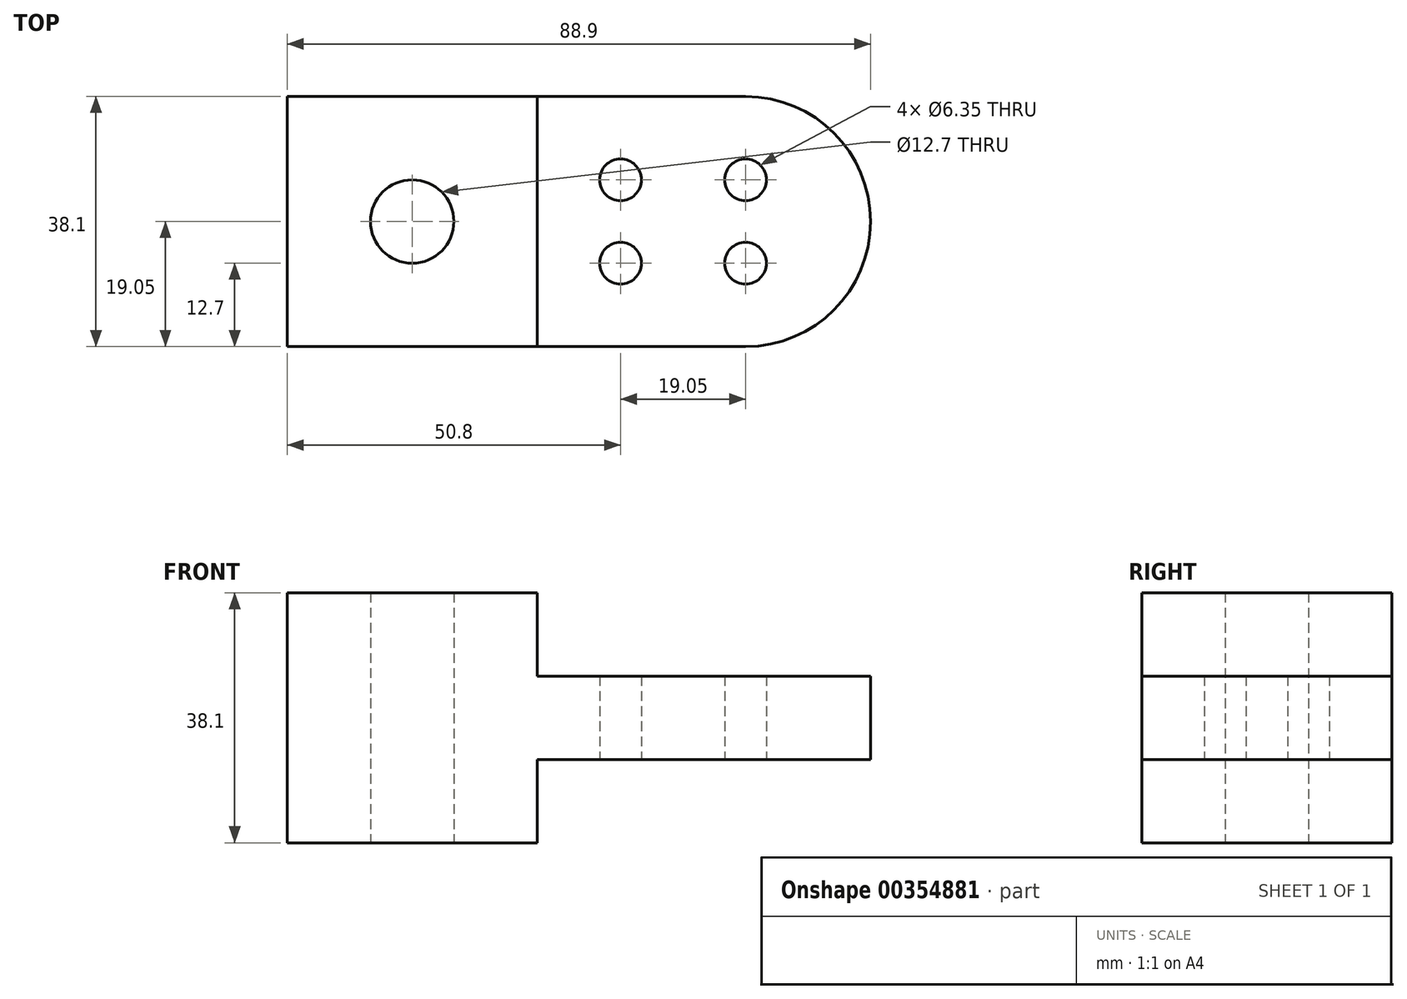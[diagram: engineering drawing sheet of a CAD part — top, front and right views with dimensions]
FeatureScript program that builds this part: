
annotation { "Feature Type Name" : "Feature", "Feature Type Description" : "" }
export const myFeature = defineFeature(function(context is Context, id is Id, definition is map)
    precondition{}
    {
        {
            var Q0;
            Q0=qCreatedBy(makeId("Top.planeOp"),FACE);
            var sketch = newSketch(context, id + "F0", { "sketchPlane" : qUnion([Q0])});
            skLineSegment(sketch, "E0", {"start": v(-19.05, -19.05) * mm, "end": v(-19.05, 19.05) * mm});
            skLineSegment(sketch, "E1", {"start": v(-19.05, 19.05) * mm, "end": v(19.05, 19.05) * mm});
            skLineSegment(sketch, "E2", {"start": v(19.05, 19.05) * mm, "end": v(19.05, -19.05) * mm});
            skLineSegment(sketch, "E3", {"start": v(19.05, -19.05) * mm, "end": v(-19.05, -19.05) * mm});
            skLineSegment(sketch, "E4", {"start": v(19.05, 19.05) * mm, "end": v(50.8, 19.05) * mm});
            skLineSegment(sketch, "E5", {"start": v(50.8, 19.05) * mm, "end": v(50.8, -19.05) * mm});
            skLineSegment(sketch, "E6", {"start": v(50.8, -19.05) * mm, "end": v(19.05, -19.05) * mm});
            skCircle(sketch, "E7", {"center": v(0, 0) * mm, "radius": 6.35 * mm});
            skCircle(sketch, "E8", {"center": v(31.75, 6.35) * mm, "radius": 3.18 * mm});
            skCircle(sketch, "E9", {"center": v(50.8, 6.35) * mm, "radius": 3.18 * mm});
            skCircle(sketch, "E10", {"center": v(50.8, -6.35) * mm, "radius": 3.18 * mm});
            skCircle(sketch, "E11", {"center": v(31.75, -6.35) * mm, "radius": 3.18 * mm});
            skArc(sketch, "E12", {"start": v(50.8, -19.05) * mm, "mid": v(69.85, 0) * mm, "end": v(50.8, 19.05) * mm});
            skSolve(sketch);
        }
        {
            var Q0;
            Q0=makeQuery(id+"F0.imprint","IMPRINT",FACE,{"disambiguationData":[TD([[makeQuery(id+"F0.imprint","IMPRINT",EDGE,{"derivedFrom":sQuery(id+"F0.wireOp",EDGE,"E0")}),-1.0]])]});
            extrude(context, id + "F1", {"entities" : qUnion([Q0]), "endBound" : BoundingType.SYMMETRIC, "depth" : 38.1 * mm});
        }
        {
            var Q0;
            Q0=makeQuery(id+"F0.imprint","IMPRINT",FACE,{"disambiguationData":[TD([[makeQuery(id+"F0.imprint","IMPRINT",EDGE,{"derivedFrom":sQuery(id+"F0.wireOp",EDGE,"E2")}),1.0]])]});
            var Q1;
            {var subQ4=sQuery(id+"F0.wireOp",EDGE,"E12");Q1=makeQuery(id+"F0.imprint","IMPRINT",FACE,{"disambiguationData":[TD([[makeQuery(id+"F0.imprint","IMPRINT",EDGE,{"derivedFrom":subQ4}),1.0]])]});}
            extrude(context, id + "F2", {"entities" : qUnion([Q0, Q1]), "operationType" : NewBodyOperationType.ADD, "endBound" : BoundingType.SYMMETRIC, "depth" : 12.7 * mm});
        }
    });
